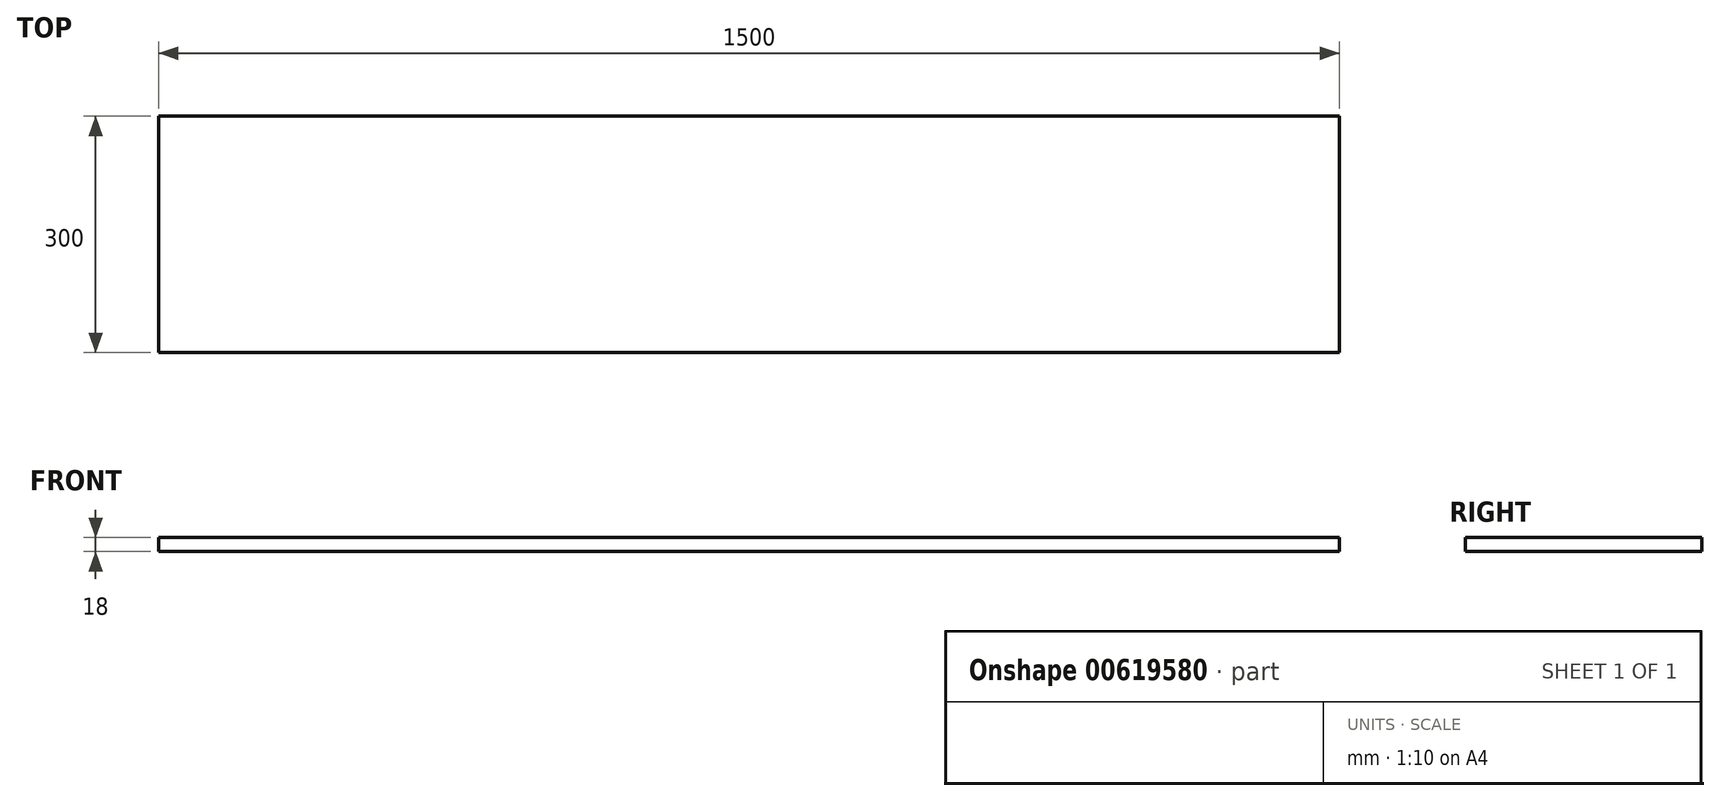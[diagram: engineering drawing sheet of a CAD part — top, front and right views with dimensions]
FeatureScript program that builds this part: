
annotation { "Feature Type Name" : "Feature", "Feature Type Description" : "" }
export const myFeature = defineFeature(function(context is Context, id is Id, definition is map)
    precondition{}
    {
        {
            var Q0;
            Q0=qCreatedBy(makeId("Top.planeOp"),FACE);
            var sketch = newSketch(context, id + "F0", { "sketchPlane" : qUnion([Q0])});
            skLineSegment(sketch, "E0.bottom", {"start": v(-751.3, 196.64) * mm, "end": v(748.7, 196.64) * mm});
            skLineSegment(sketch, "E0.top", {"start": v(-751.3, -103.36) * mm, "end": v(748.7, -103.36) * mm});
            skLineSegment(sketch, "E0.left", {"start": v(-751.3, 196.64) * mm, "end": v(-751.3, -103.36) * mm});
            skLineSegment(sketch, "E0.right", {"start": v(748.7, 196.64) * mm, "end": v(748.7, -103.36) * mm});
            skSolve(sketch);
        }
        {
            var Q0;
            Q0=makeQuery(id+"F0.imprint","IMPRINT",FACE,{"disambiguationData":[TD([[makeQuery(id+"F0.imprint","IMPRINT",EDGE,{"derivedFrom":sQuery(id+"F0.wireOp",EDGE,"E0.bottom")}),-1.0]])]});
            extrude(context, id + "F1", {"entities" : qUnion([Q0]), "depth" : 18 * mm, "offsetDistance" : 25 * mm});
        }
    });
